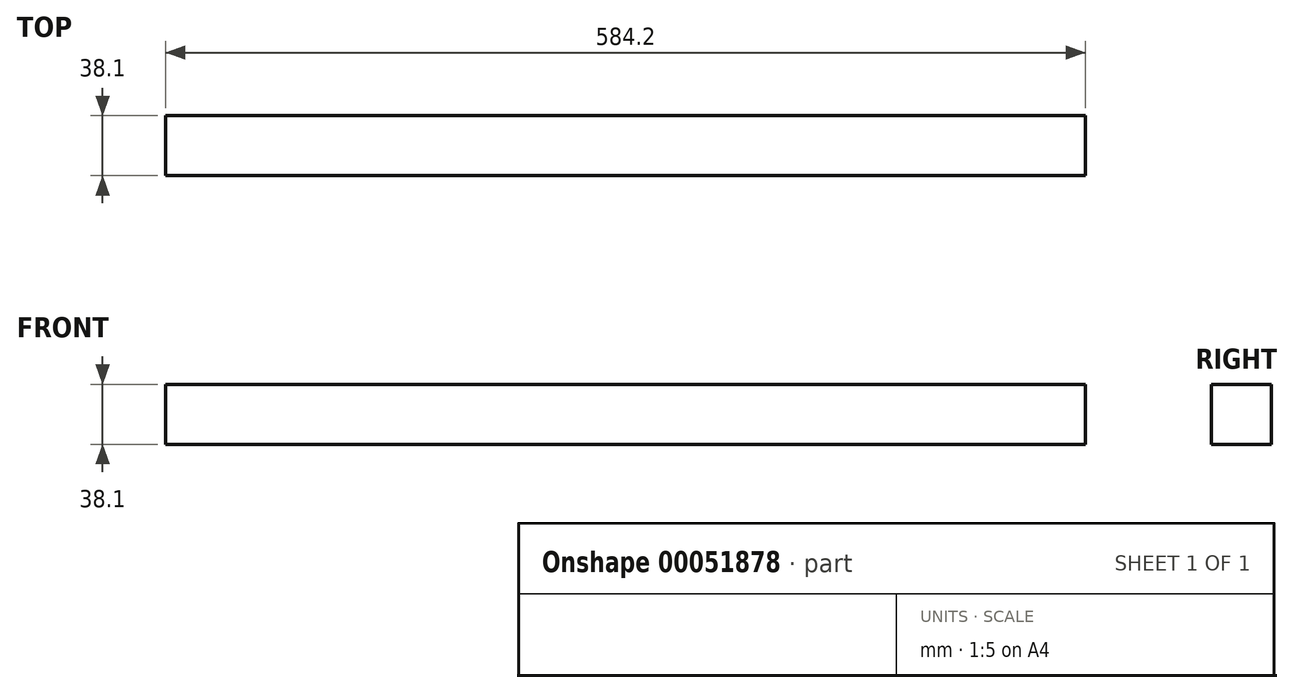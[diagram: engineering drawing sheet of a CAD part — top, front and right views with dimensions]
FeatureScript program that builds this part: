
annotation { "Feature Type Name" : "Feature", "Feature Type Description" : "" }
export const myFeature = defineFeature(function(context is Context, id is Id, definition is map)
    precondition{}
    {
        {
            var Q0;
            Q0=qCreatedBy(makeId("Right.planeOp"),FACE);
            var sketch = newSketch(context, id + "F0", { "sketchPlane" : qUnion([Q0])});
            skLineSegment(sketch, "E0.bottom", {"start": v(-19.05, 25.4) * mm, "end": v(19.05, 25.4) * mm});
            skLineSegment(sketch, "E0.top", {"start": v(-19.05, -12.7) * mm, "end": v(19.05, -12.7) * mm});
            skLineSegment(sketch, "E0.left", {"start": v(-19.05, 25.4) * mm, "end": v(-19.05, -12.7) * mm});
            skLineSegment(sketch, "E0.right", {"start": v(19.05, 25.4) * mm, "end": v(19.05, -12.7) * mm});
            skSolve(sketch);
        }
        {
            var Q0;
            Q0=makeQuery(id+"F0.imprint","IMPRINT",FACE,{"disambiguationData":[TD([[makeQuery(id+"F0.imprint","IMPRINT",EDGE,{"derivedFrom":sQuery(id+"F0.wireOp",EDGE,"E0.bottom")}),-1.0]])]});
            extrude(context, id + "F1", {"entities" : qUnion([Q0]), "depth" : 584.2 * mm});
        }
    });
